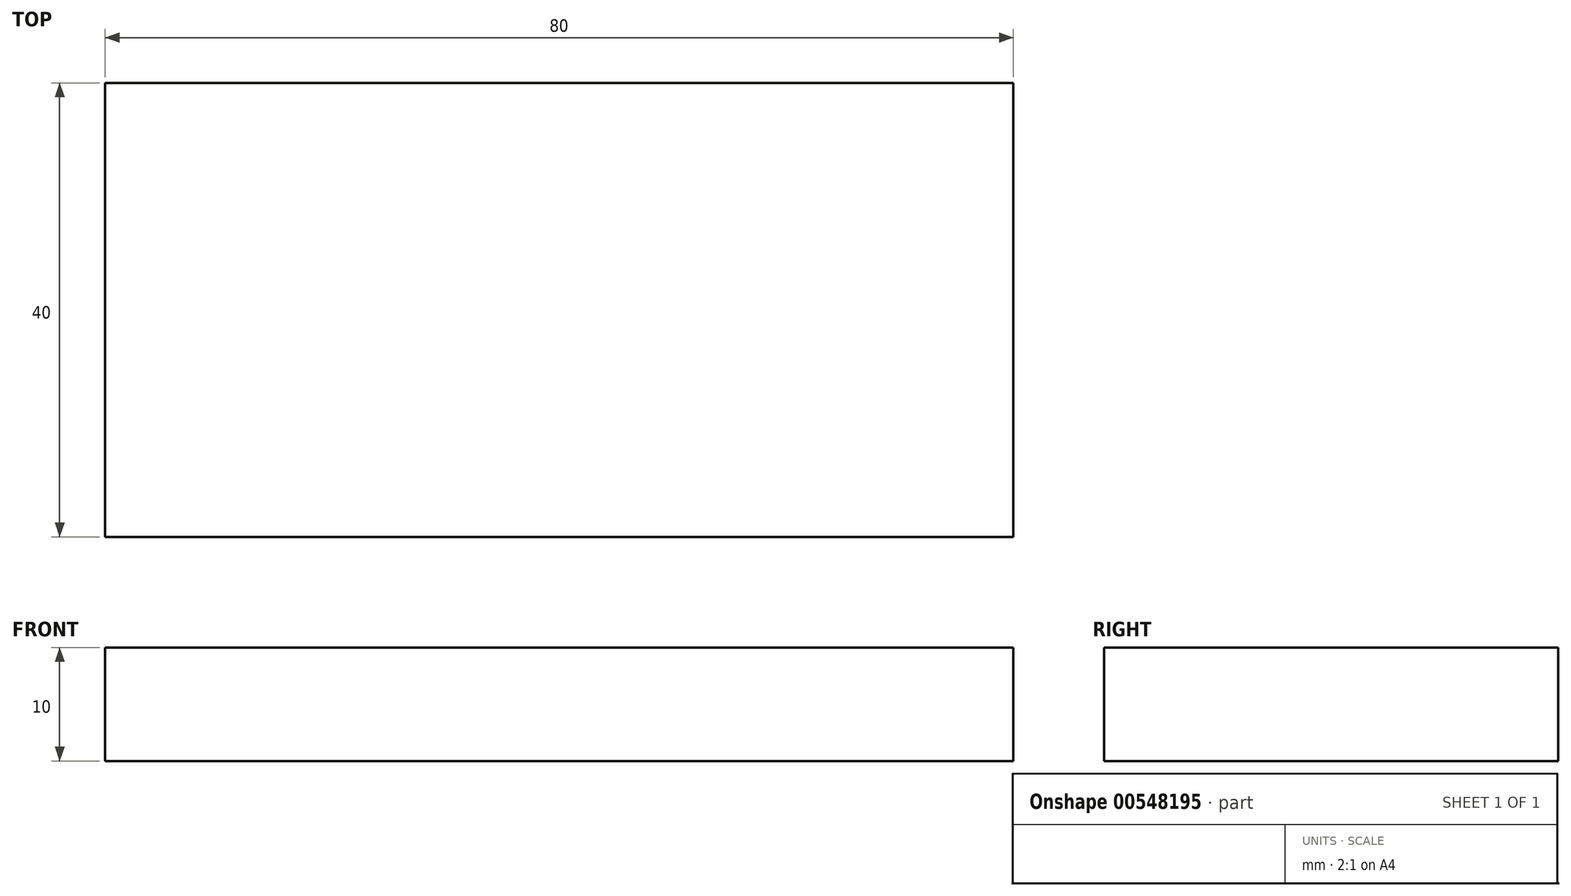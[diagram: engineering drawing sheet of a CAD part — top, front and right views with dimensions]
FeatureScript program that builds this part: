
annotation { "Feature Type Name" : "Feature", "Feature Type Description" : "" }
export const myFeature = defineFeature(function(context is Context, id is Id, definition is map)
    precondition{}
    {
        {
            var Q0;
            Q0=qCreatedBy(makeId("Top.planeOp"),FACE);
            var sketch = newSketch(context, id + "F0", { "sketchPlane" : qUnion([Q0])});
            skLineSegment(sketch, "E0.bottom", {"start": v(0, 0) * mm, "end": v(80, 0) * mm});
            skLineSegment(sketch, "E0.top", {"start": v(0, 40) * mm, "end": v(80, 40) * mm});
            skLineSegment(sketch, "E0.left", {"start": v(0, 0) * mm, "end": v(0, 40) * mm});
            skLineSegment(sketch, "E0.right", {"start": v(80, 0) * mm, "end": v(80, 40) * mm});
            skSolve(sketch);
        }
        {
            var Q0;
            Q0=makeQuery(id+"F0.imprint","IMPRINT",FACE,{"disambiguationData":[TD([[makeQuery(id+"F0.imprint","IMPRINT",EDGE,{"derivedFrom":sQuery(id+"F0.wireOp",EDGE,"E0.bottom")}),1.0]])]});
            extrude(context, id + "F1", {"entities" : qUnion([Q0]), "depth" : 10 * mm, "offsetDistance" : 25 * mm});
        }
    });
